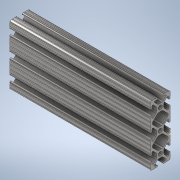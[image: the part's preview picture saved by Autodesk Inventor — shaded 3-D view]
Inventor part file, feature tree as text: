
AUTODESK INVENTOR PART (.ipt)
format: ipt  version: 2020 (Build 240168000, 168)  size: 374,784 bytes
history: native  units: in
note: dims shown in document units (in); Inventor stores cm internally (conversion verified against a paired STEP export)
features: sketch x2, extrude x1
ambient origin geometry x8: Origin, YZ Plane, XZ Plane, XY Plane, X Axis, Y Axis, Z Axis, Center Point
bodies: Solid1 (feature_tree)
feature tree (3):
  extrude  "Extrusion1"  [1 undecoded]
  sketch  "Sketch2"
  sketch  "Sketch1"  dims[d0=7.0in d1=0.0in]
note: 1 required parameter value undecoded (feature->parameter linkage not recoverable at this tier; creation-order binding heuristic only, values carry confidence <= 0.55)
